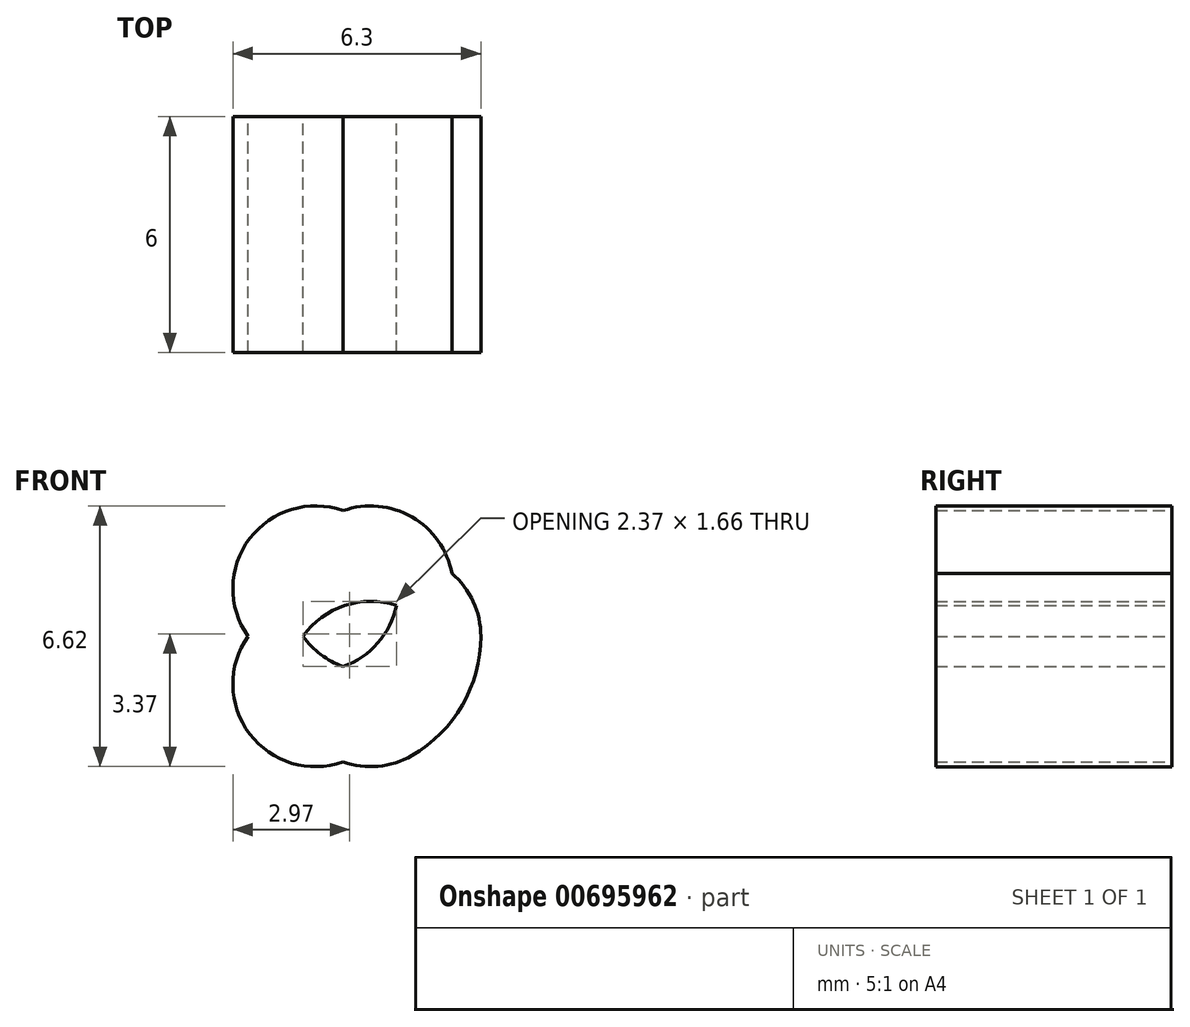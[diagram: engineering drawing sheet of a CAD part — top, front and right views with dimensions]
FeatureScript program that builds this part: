
annotation { "Feature Type Name" : "Feature", "Feature Type Description" : "" }
export const myFeature = defineFeature(function(context is Context, id is Id, definition is map)
    precondition{}
    {
        {
            var Q0;
            Q0=qCreatedBy(makeId("Front.planeOp"),FACE);
            var sketch = newSketch(context, id + "F0", { "sketchPlane" : qUnion([Q0])});
            skCircle(sketch, "E0", {"center": v(0, 0) * mm, "radius": 3.5 * mm});
            skCircle(sketch, "E1", {"center": v(1.4, 0) * mm, "radius": 2.1 * mm});
            skCircle(sketch, "E2", {"center": v(0.7, 1.21) * mm, "radius": 2.1 * mm});
            skCircle(sketch, "E3", {"center": v(-0.7, 1.21) * mm, "radius": 2.1 * mm});
            skCircle(sketch, "E4", {"center": v(-1.4, 0) * mm, "radius": 2.1 * mm});
            skPoint(sketch, "E5", {"position": v(-2.76, 1.6) * mm});
            skPoint(sketch, "E6", {"position": v(0, 3.2) * mm});
            skPoint(sketch, "E7", {"position": v(2.76, 1.6) * mm});
            skCircle(sketch, "E8", {"center": v(-0.7, -1.21) * mm, "radius": 2.1 * mm});
            skCircle(sketch, "E9", {"center": v(0.7, -1.21) * mm, "radius": 2.1 * mm});
            skSolve(sketch);
        }
        {
            var Q0;
            {var subQ0=sQuery(id+"F0.wireOp",EDGE,"E4");var subQ1=sQuery(id+"F0.wireOp",EDGE,"E3");var subQ2=makeQuery(id+"F0.imprint","INTERSECT",VERTEX,{"disambiguationData":[OD(0.0)],"derivedFrom":[subQ1,subQ0]});Q0=makeQuery(id+"F0.imprint","IMPRINT",FACE,{"disambiguationData":[TD([[makeQuery(id+"F0.imprint","IMPRINT",EDGE,{"disambiguationData":[TD([[subQ2,-1.0]])],"derivedFrom":subQ1}),-1.0]])]});}
            var Q1;
            {var subQ0=sQuery(id+"F0.wireOp",EDGE,"E4");var subQ1=sQuery(id+"F0.wireOp",EDGE,"E2");var subQ2=makeQuery(id+"F0.imprint","INTERSECT",VERTEX,{"disambiguationData":[OD(0.0)],"derivedFrom":[subQ1,subQ0]});Q1=makeQuery(id+"F0.imprint","IMPRINT",FACE,{"disambiguationData":[TD([[makeQuery(id+"F0.imprint","IMPRINT",EDGE,{"disambiguationData":[TD([[subQ2,-1.0]])],"derivedFrom":subQ1}),-1.0]])]});}
            var Q2;
            {var subQ0=sQuery(id+"F0.wireOp",EDGE,"E3");var subQ1=sQuery(id+"F0.wireOp",EDGE,"E2");var subQ2=makeQuery(id+"F0.imprint","INTERSECT",VERTEX,{"disambiguationData":[OD(0.0)],"derivedFrom":[subQ1,subQ0]});Q2=makeQuery(id+"F0.imprint","IMPRINT",FACE,{"disambiguationData":[TD([[makeQuery(id+"F0.imprint","IMPRINT",EDGE,{"disambiguationData":[TD([[subQ2,-1.0]])],"derivedFrom":subQ1}),-1.0]])]});}
            var Q3;
            {var subQ0=sQuery(id+"F0.wireOp",EDGE,"E3");var subQ1=sQuery(id+"F0.wireOp",EDGE,"E1");var subQ2=makeQuery(id+"F0.imprint","INTERSECT",VERTEX,{"disambiguationData":[OD(0.0)],"derivedFrom":[subQ1,subQ0]});Q3=makeQuery(id+"F0.imprint","IMPRINT",FACE,{"disambiguationData":[TD([[makeQuery(id+"F0.imprint","IMPRINT",EDGE,{"disambiguationData":[TD([[subQ2,-1.0]])],"derivedFrom":subQ1}),-1.0]])]});}
            var Q4;
            {var subQ0=sQuery(id+"F0.wireOp",EDGE,"E2");var subQ1=sQuery(id+"F0.wireOp",EDGE,"E1");var subQ2=makeQuery(id+"F0.imprint","INTERSECT",VERTEX,{"disambiguationData":[OD(0.0)],"derivedFrom":[subQ1,subQ0]});Q4=makeQuery(id+"F0.imprint","IMPRINT",FACE,{"disambiguationData":[TD([[makeQuery(id+"F0.imprint","IMPRINT",EDGE,{"disambiguationData":[TD([[subQ2,-1.0]])],"derivedFrom":subQ1}),-1.0]])]});}
            var Q5;
            {var subQ0=sQuery(id+"F0.wireOp",EDGE,"E2");var subQ1=sQuery(id+"F0.wireOp",EDGE,"E1");var subQ2=makeQuery(id+"F0.imprint","INTERSECT",VERTEX,{"disambiguationData":[OD(0.0)],"derivedFrom":[subQ1,subQ0]});Q5=makeQuery(id+"F0.imprint","IMPRINT",FACE,{"disambiguationData":[TD([[makeQuery(id+"F0.imprint","IMPRINT",EDGE,{"disambiguationData":[TD([[subQ2,-1.0]])],"derivedFrom":subQ1}),1.0]])]});}
            var Q6;
            {var subQ0=sQuery(id+"F0.wireOp",EDGE,"E1");var subQ1=makeQuery(id+"F0.imprint","INTERSECT",VERTEX,{"derivedFrom":[sQuery(id+"F0.wireOp",EDGE,"E0"),subQ0]});Q6=makeQuery(id+"F0.imprint","IMPRINT",FACE,{"disambiguationData":[TD([[makeQuery(id+"F0.imprint","IMPRINT",EDGE,{"disambiguationData":[TD([[subQ1,-1.0]])],"derivedFrom":subQ0}),1.0]])]});}
            var Q7;
            {var subQ0=sQuery(id+"F0.wireOp",EDGE,"E8");var subQ1=sQuery(id+"F0.wireOp",EDGE,"E1");var subQ2=makeQuery(id+"F0.imprint","INTERSECT",VERTEX,{"disambiguationData":[OD(1.0)],"derivedFrom":[subQ1,subQ0]});Q7=makeQuery(id+"F0.imprint","IMPRINT",FACE,{"disambiguationData":[TD([[makeQuery(id+"F0.imprint","IMPRINT",EDGE,{"disambiguationData":[TD([[subQ2,-1.0]])],"derivedFrom":subQ1}),-1.0]])]});}
            var Q8;
            {var subQ0=sQuery(id+"F0.wireOp",EDGE,"E3");var subQ1=sQuery(id+"F0.wireOp",EDGE,"E1");var subQ2=makeQuery(id+"F0.imprint","INTERSECT",VERTEX,{"disambiguationData":[OD(1.0)],"derivedFrom":[subQ1,subQ0]});Q8=makeQuery(id+"F0.imprint","IMPRINT",FACE,{"disambiguationData":[TD([[makeQuery(id+"F0.imprint","IMPRINT",EDGE,{"disambiguationData":[TD([[subQ2,-1.0]])],"derivedFrom":subQ1}),-1.0]])]});}
            var Q9;
            {var subQ0=sQuery(id+"F0.wireOp",EDGE,"E8");var subQ1=sQuery(id+"F0.wireOp",EDGE,"E4");var subQ2=makeQuery(id+"F0.imprint","INTERSECT",VERTEX,{"disambiguationData":[OD(1.0)],"derivedFrom":[subQ1,subQ0]});Q9=makeQuery(id+"F0.imprint","IMPRINT",FACE,{"disambiguationData":[TD([[makeQuery(id+"F0.imprint","IMPRINT",EDGE,{"disambiguationData":[TD([[subQ2,-1.0]])],"derivedFrom":subQ1}),-1.0]])]});}
            var Q10;
            {var subQ0=sQuery(id+"F0.wireOp",EDGE,"E8");var subQ1=sQuery(id+"F0.wireOp",EDGE,"E3");var subQ2=makeQuery(id+"F0.imprint","INTERSECT",VERTEX,{"disambiguationData":[OD(0.0)],"derivedFrom":[subQ1,subQ0]});Q10=makeQuery(id+"F0.imprint","IMPRINT",FACE,{"disambiguationData":[TD([[makeQuery(id+"F0.imprint","IMPRINT",EDGE,{"disambiguationData":[TD([[subQ2,-1.0]])],"derivedFrom":subQ1}),-1.0]])]});}
            var Q11;
            {var subQ0=sQuery(id+"F0.wireOp",EDGE,"E4");var subQ1=sQuery(id+"F0.wireOp",EDGE,"E1");var subQ2=makeQuery(id+"F0.imprint","INTERSECT",VERTEX,{"disambiguationData":[OD(1.0)],"derivedFrom":[subQ1,subQ0]});Q11=makeQuery(id+"F0.imprint","IMPRINT",FACE,{"disambiguationData":[TD([[makeQuery(id+"F0.imprint","IMPRINT",EDGE,{"disambiguationData":[TD([[subQ2,-1.0]])],"derivedFrom":subQ1}),-1.0]])]});}
            var Q12;
            {var subQ0=sQuery(id+"F0.wireOp",EDGE,"E4");var subQ1=sQuery(id+"F0.wireOp",EDGE,"E1");var subQ2=makeQuery(id+"F0.imprint","INTERSECT",VERTEX,{"disambiguationData":[OD(1.0)],"derivedFrom":[subQ1,subQ0]});Q12=makeQuery(id+"F0.imprint","IMPRINT",FACE,{"disambiguationData":[TD([[makeQuery(id+"F0.imprint","IMPRINT",EDGE,{"disambiguationData":[TD([[subQ2,-1.0]])],"derivedFrom":subQ1}),1.0]])]});}
            var Q13;
            {var subQ0=sQuery(id+"F0.wireOp",EDGE,"E8");var subQ1=sQuery(id+"F0.wireOp",EDGE,"E1");var subQ2=makeQuery(id+"F0.imprint","INTERSECT",VERTEX,{"disambiguationData":[OD(1.0)],"derivedFrom":[subQ1,subQ0]});Q13=makeQuery(id+"F0.imprint","IMPRINT",FACE,{"disambiguationData":[TD([[makeQuery(id+"F0.imprint","IMPRINT",EDGE,{"disambiguationData":[TD([[subQ2,-1.0]])],"derivedFrom":subQ1}),1.0]])]});}
            var Q14;
            {var subQ0=sQuery(id+"F0.wireOp",EDGE,"E8");var subQ1=sQuery(id+"F0.wireOp",EDGE,"E2");var subQ2=makeQuery(id+"F0.imprint","INTERSECT",VERTEX,{"disambiguationData":[OD(1.0)],"derivedFrom":[subQ1,subQ0]});Q14=makeQuery(id+"F0.imprint","IMPRINT",FACE,{"disambiguationData":[TD([[makeQuery(id+"F0.imprint","IMPRINT",EDGE,{"disambiguationData":[TD([[subQ2,-1.0]])],"derivedFrom":subQ1}),1.0]])]});}
            var Q15;
            {var subQ0=sQuery(id+"F0.wireOp",EDGE,"E3");var subQ1=sQuery(id+"F0.wireOp",EDGE,"E1");var subQ2=makeQuery(id+"F0.imprint","INTERSECT",VERTEX,{"disambiguationData":[OD(0.0)],"derivedFrom":[subQ1,subQ0]});Q15=makeQuery(id+"F0.imprint","IMPRINT",FACE,{"disambiguationData":[TD([[makeQuery(id+"F0.imprint","IMPRINT",EDGE,{"disambiguationData":[TD([[subQ2,-1.0]])],"derivedFrom":subQ1}),1.0]])]});}
            var Q16;
            {var subQ0=sQuery(id+"F0.wireOp",EDGE,"E4");var subQ1=sQuery(id+"F0.wireOp",EDGE,"E1");var subQ2=makeQuery(id+"F0.imprint","INTERSECT",VERTEX,{"disambiguationData":[OD(0.0)],"derivedFrom":[subQ1,subQ0]});Q16=makeQuery(id+"F0.imprint","IMPRINT",FACE,{"disambiguationData":[TD([[makeQuery(id+"F0.imprint","IMPRINT",EDGE,{"disambiguationData":[TD([[subQ2,-1.0]])],"derivedFrom":subQ1}),-1.0]])]});}
            var Q17;
            {var subQ0=sQuery(id+"F0.wireOp",EDGE,"E8");var subQ1=sQuery(id+"F0.wireOp",EDGE,"E2");var subQ2=makeQuery(id+"F0.imprint","INTERSECT",VERTEX,{"disambiguationData":[OD(0.0)],"derivedFrom":[subQ1,subQ0]});Q17=makeQuery(id+"F0.imprint","IMPRINT",FACE,{"disambiguationData":[TD([[makeQuery(id+"F0.imprint","IMPRINT",EDGE,{"disambiguationData":[TD([[subQ2,-1.0]])],"derivedFrom":subQ1}),-1.0]])]});}
            var Q18;
            {var subQ0=sQuery(id+"F0.wireOp",EDGE,"E2");var subQ1=sQuery(id+"F0.wireOp",EDGE,"E1");var subQ2=makeQuery(id+"F0.imprint","INTERSECT",VERTEX,{"disambiguationData":[OD(1.0)],"derivedFrom":[subQ1,subQ0]});Q18=makeQuery(id+"F0.imprint","IMPRINT",FACE,{"disambiguationData":[TD([[makeQuery(id+"F0.imprint","IMPRINT",EDGE,{"disambiguationData":[TD([[subQ2,-1.0]])],"derivedFrom":subQ1}),-1.0]])]});}
            var Q19;
            {var subQ0=sQuery(id+"F0.wireOp",EDGE,"E3");var subQ1=sQuery(id+"F0.wireOp",EDGE,"E1");var subQ2=makeQuery(id+"F0.imprint","INTERSECT",VERTEX,{"disambiguationData":[OD(1.0)],"derivedFrom":[subQ1,subQ0]});Q19=makeQuery(id+"F0.imprint","IMPRINT",FACE,{"disambiguationData":[TD([[makeQuery(id+"F0.imprint","IMPRINT",EDGE,{"disambiguationData":[TD([[subQ2,-1.0]])],"derivedFrom":subQ1}),1.0]])]});}
            var Q20;
            {var subQ7=sQuery(id+"F0.wireOp",EDGE,"E1");var subQ9=sQuery(id+"F0.wireOp",EDGE,"E9");var subQ10=makeQuery(id+"F0.imprint","INTERSECT",VERTEX,{"disambiguationData":[OD(0.0)],"derivedFrom":[subQ7,subQ9]});Q20=makeQuery(id+"F0.imprint","IMPRINT",FACE,{"disambiguationData":[TD([[makeQuery(id+"F0.imprint","IMPRINT",EDGE,{"disambiguationData":[TD([[subQ10,-1.0]])],"derivedFrom":subQ7}),1.0]])]});}
            var Q21;
            {var subQ0=sQuery(id+"F0.wireOp",EDGE,"E4");var subQ1=sQuery(id+"F0.wireOp",EDGE,"E1");var subQ2=makeQuery(id+"F0.imprint","INTERSECT",VERTEX,{"disambiguationData":[OD(0.0)],"derivedFrom":[subQ1,subQ0]});Q21=makeQuery(id+"F0.imprint","IMPRINT",FACE,{"disambiguationData":[TD([[makeQuery(id+"F0.imprint","IMPRINT",EDGE,{"disambiguationData":[TD([[subQ2,-1.0]])],"derivedFrom":subQ1}),1.0]])]});}
            var Q22;
            {var subQ0=sQuery(id+"F0.wireOp",EDGE,"E8");var subQ1=sQuery(id+"F0.wireOp",EDGE,"E1");var subQ2=makeQuery(id+"F0.imprint","INTERSECT",VERTEX,{"disambiguationData":[OD(0.0)],"derivedFrom":[subQ1,subQ0]});Q22=makeQuery(id+"F0.imprint","IMPRINT",FACE,{"disambiguationData":[TD([[makeQuery(id+"F0.imprint","IMPRINT",EDGE,{"disambiguationData":[TD([[subQ2,-1.0]])],"derivedFrom":subQ1}),-1.0]])]});}
            var Q23;
            {var subQ0=sQuery(id+"F0.wireOp",EDGE,"E9");var subQ1=sQuery(id+"F0.wireOp",EDGE,"E1");var subQ2=makeQuery(id+"F0.imprint","INTERSECT",VERTEX,{"disambiguationData":[OD(0.0)],"derivedFrom":[subQ1,subQ0]});Q23=makeQuery(id+"F0.imprint","IMPRINT",FACE,{"disambiguationData":[TD([[makeQuery(id+"F0.imprint","IMPRINT",EDGE,{"disambiguationData":[TD([[subQ2,-1.0]])],"derivedFrom":subQ1}),-1.0]])]});}
            var Q24;
            {var subQ0=sQuery(id+"F0.wireOp",EDGE,"E2");var subQ1=sQuery(id+"F0.wireOp",EDGE,"E1");var subQ2=makeQuery(id+"F0.imprint","INTERSECT",VERTEX,{"disambiguationData":[OD(1.0)],"derivedFrom":[subQ1,subQ0]});Q24=makeQuery(id+"F0.imprint","IMPRINT",FACE,{"disambiguationData":[TD([[makeQuery(id+"F0.imprint","IMPRINT",EDGE,{"disambiguationData":[TD([[subQ2,-1.0]])],"derivedFrom":subQ1}),1.0]])]});}
            var Q25;
            {var subQ0=sQuery(id+"F0.wireOp",EDGE,"E4");var subQ1=sQuery(id+"F0.wireOp",EDGE,"E3");var subQ2=makeQuery(id+"F0.imprint","INTERSECT",VERTEX,{"disambiguationData":[OD(1.0)],"derivedFrom":[subQ1,subQ0]});Q25=makeQuery(id+"F0.imprint","IMPRINT",FACE,{"disambiguationData":[TD([[makeQuery(id+"F0.imprint","IMPRINT",EDGE,{"disambiguationData":[TD([[subQ2,-1.0]])],"derivedFrom":subQ1}),1.0]])]});}
            var Q26;
            {var subQ0=sQuery(id+"F0.wireOp",EDGE,"E8");var subQ1=sQuery(id+"F0.wireOp",EDGE,"E3");var subQ2=makeQuery(id+"F0.imprint","INTERSECT",VERTEX,{"disambiguationData":[OD(1.0)],"derivedFrom":[subQ1,subQ0]});Q26=makeQuery(id+"F0.imprint","IMPRINT",FACE,{"disambiguationData":[TD([[makeQuery(id+"F0.imprint","IMPRINT",EDGE,{"disambiguationData":[TD([[subQ2,-1.0]])],"derivedFrom":subQ1}),1.0]])]});}
            var Q27;
            {var subQ0=sQuery(id+"F0.wireOp",EDGE,"E8");var subQ1=sQuery(id+"F0.wireOp",EDGE,"E1");var subQ2=makeQuery(id+"F0.imprint","INTERSECT",VERTEX,{"disambiguationData":[OD(0.0)],"derivedFrom":[subQ1,subQ0]});Q27=makeQuery(id+"F0.imprint","IMPRINT",FACE,{"disambiguationData":[TD([[makeQuery(id+"F0.imprint","IMPRINT",EDGE,{"disambiguationData":[TD([[subQ2,-1.0]])],"derivedFrom":subQ1}),1.0]])]});}
            var Q28;
            {var subQ0=sQuery(id+"F0.wireOp",EDGE,"E9");var subQ1=sQuery(id+"F0.wireOp",EDGE,"E4");var subQ2=makeQuery(id+"F0.imprint","INTERSECT",VERTEX,{"disambiguationData":[OD(0.0)],"derivedFrom":[subQ1,subQ0]});Q28=makeQuery(id+"F0.imprint","IMPRINT",FACE,{"disambiguationData":[TD([[makeQuery(id+"F0.imprint","IMPRINT",EDGE,{"disambiguationData":[TD([[subQ2,1.0]])],"derivedFrom":subQ1}),1.0]])]});}
            var Q29;
            {var subQ0=sQuery(id+"F0.wireOp",EDGE,"E4");var subQ1=sQuery(id+"F0.wireOp",EDGE,"E2");var subQ2=makeQuery(id+"F0.imprint","INTERSECT",VERTEX,{"disambiguationData":[OD(1.0)],"derivedFrom":[subQ1,subQ0]});Q29=makeQuery(id+"F0.imprint","IMPRINT",FACE,{"disambiguationData":[TD([[makeQuery(id+"F0.imprint","IMPRINT",EDGE,{"disambiguationData":[TD([[subQ2,-1.0]])],"derivedFrom":subQ1}),1.0]])]});}
            var Q30;
            {var subQ0=sQuery(id+"F0.wireOp",EDGE,"E3");var subQ1=sQuery(id+"F0.wireOp",EDGE,"E2");var subQ2=makeQuery(id+"F0.imprint","INTERSECT",VERTEX,{"disambiguationData":[OD(1.0)],"derivedFrom":[subQ1,subQ0]});Q30=makeQuery(id+"F0.imprint","IMPRINT",FACE,{"disambiguationData":[TD([[makeQuery(id+"F0.imprint","IMPRINT",EDGE,{"disambiguationData":[TD([[subQ2,-1.0]])],"derivedFrom":subQ1}),1.0]])]});}
            extrude(context, id + "F1", {"entities" : qUnion([Q0, Q1, Q2, Q3, Q4, Q5, Q6, Q7, Q8, Q9, Q10, Q11, Q12, Q13, Q14, Q15, Q16, Q17, Q18, Q19, Q20, Q21, Q22, Q23, Q24, Q25, Q26, Q27, Q28, Q29, Q30]), "depth" : 6 * mm, "offsetDistance" : 25 * mm});
        }
    });
